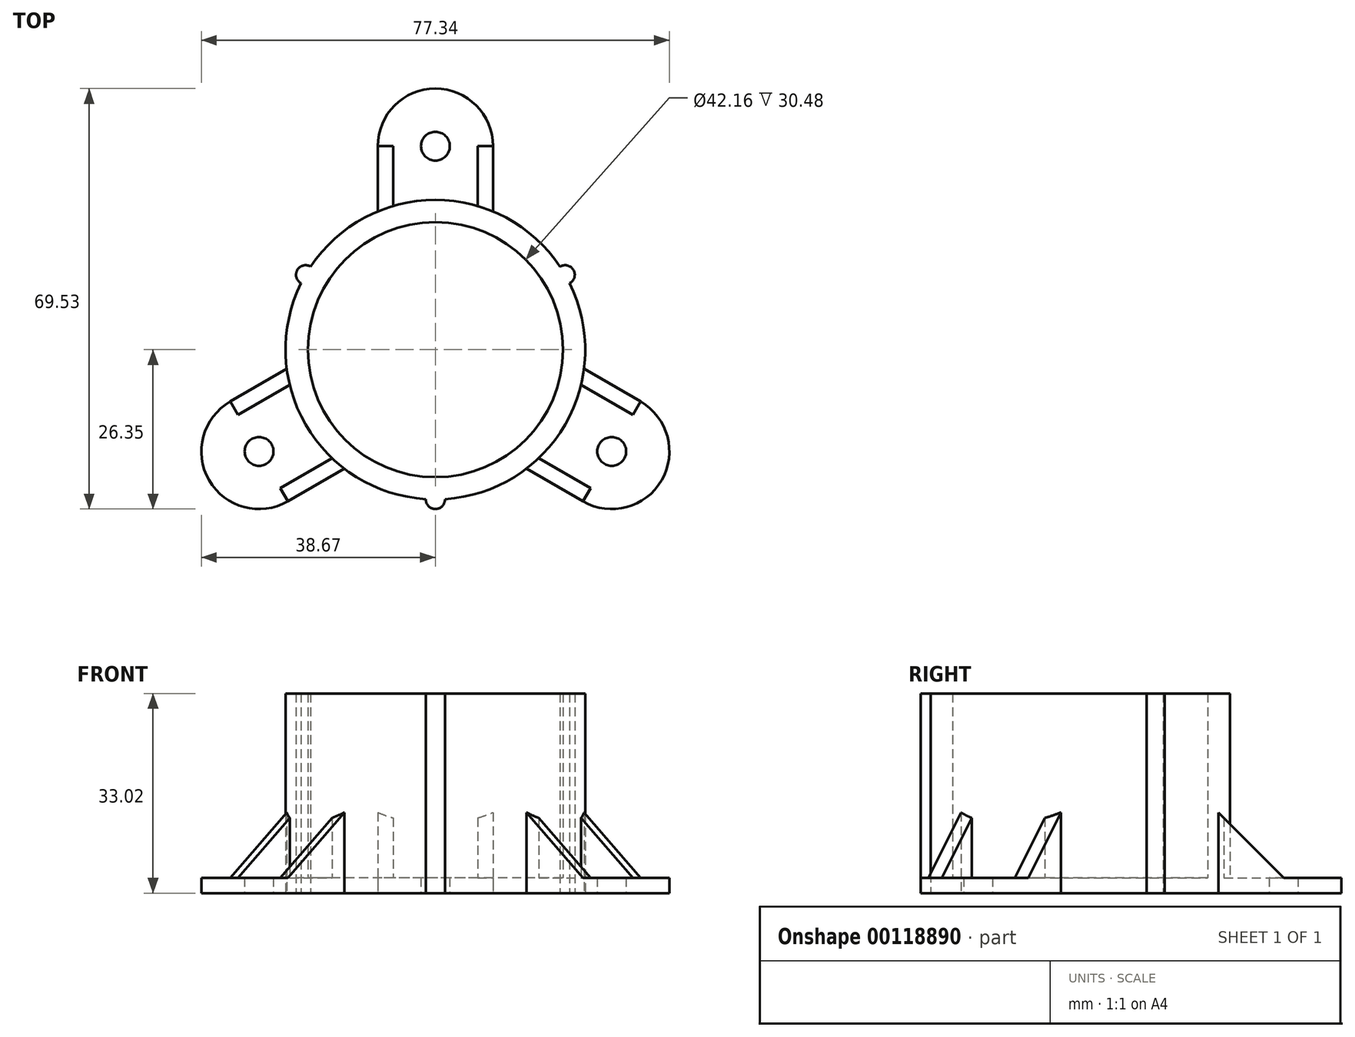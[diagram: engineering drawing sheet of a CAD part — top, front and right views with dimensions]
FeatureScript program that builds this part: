
annotation { "Feature Type Name" : "Feature", "Feature Type Description" : "" }
export const myFeature = defineFeature(function(context is Context, id is Id, definition is map)
    precondition{}
    {
        {
            var Q0;
            Q0=qCreatedBy(makeId("Top.planeOp"),FACE);
            var sketch = newSketch(context, id + "F0", { "sketchPlane" : qUnion([Q0])});
            skCircle(sketch, "E0", {"center": v(0, 0) * mm, "radius": 21.08 * mm});
            skCircle(sketch, "E1", {"center": v(0, 0) * mm, "radius": 24.77 * mm});
            skCircle(sketch, "E2", {"center": v(0, -24.77) * mm, "radius": 1.59 * mm});
            skCircle(sketch, "E3.1.0", {"center": v(21.45, 12.38) * mm, "radius": 1.59 * mm});
            skCircle(sketch, "E3.2.0", {"center": v(-21.45, 12.38) * mm, "radius": 1.59 * mm});
            skLineSegment(sketch, "E4.bottom", {"start": v(-9.53, 22.86) * mm, "end": v(9.53, 22.86) * mm});
            skLineSegment(sketch, "E4.top", {"start": v(0, 43.18) * mm, "end": v(0, 43.18) * mm});
            skLineSegment(sketch, "E4.left", {"start": v(-9.53, 22.86) * mm, "end": v(-9.53, 33.66) * mm});
            skLineSegment(sketch, "E4.right", {"start": v(9.52, 22.86) * mm, "end": v(9.52, 33.66) * mm});
            skLineSegment(sketch, "E5", {"start": v(0, 13) * mm, "end": v(0, 41.76) * mm, "construction": true});
            skPoint(sketch, "E6.visualSharp", {"position": v(-9.53, 43.18) * mm});
            skArc(sketch, "E6.filletArc", {"start": v(0, 43.18) * mm, "mid": v(-6.74, 40.4) * mm, "end": v(-9.53, 33.66) * mm});
            skPoint(sketch, "E7.visualSharp", {"position": v(9.53, 43.18) * mm});
            skArc(sketch, "E7.filletArc", {"start": v(9.53, 33.66) * mm, "mid": v(6.74, 40.4) * mm, "end": v(0, 43.18) * mm});
            skCircle(sketch, "E8", {"center": v(0, 33.66) * mm, "radius": 2.38 * mm});
            skArc(sketch, "E9.1.0", {"start": v(-33.9, -8.58) * mm, "mid": v(-38.35, -14.36) * mm, "end": v(-37.4, -21.59) * mm});
            skArc(sketch, "E9.1.1", {"start": v(-37.4, -21.6) * mm, "mid": v(-31.61, -26.03) * mm, "end": v(-24.38, -25.08) * mm});
            skCircle(sketch, "E9.1.2", {"center": v(-29.15, -16.83) * mm, "radius": 2.38 * mm});
            skLineSegment(sketch, "E9.1.3", {"start": v(-24.56, -3.18) * mm, "end": v(-33.9, -8.58) * mm});
            skLineSegment(sketch, "E9.1.4", {"start": v(-15.03, -19.68) * mm, "end": v(-24.38, -25.08) * mm});
            skLineSegment(sketch, "E9.1.5", {"start": v(-15.03, -19.68) * mm, "end": v(-24.56, -3.18) * mm});
            skArc(sketch, "E9.2.0", {"start": v(24.38, -25.08) * mm, "mid": v(31.61, -26.03) * mm, "end": v(37.4, -21.6) * mm});
            skArc(sketch, "E9.2.1", {"start": v(37.4, -21.6) * mm, "mid": v(38.35, -14.36) * mm, "end": v(33.9, -8.58) * mm});
            skCircle(sketch, "E9.2.2", {"center": v(29.15, -16.83) * mm, "radius": 2.38 * mm});
            skLineSegment(sketch, "E9.2.3", {"start": v(15.03, -19.68) * mm, "end": v(24.38, -25.08) * mm});
            skLineSegment(sketch, "E9.2.4", {"start": v(24.56, -3.18) * mm, "end": v(33.9, -8.58) * mm});
            skLineSegment(sketch, "E9.2.5", {"start": v(24.56, -3.18) * mm, "end": v(15.03, -19.68) * mm});
            skSolve(sketch);
        }
        {
            var Q0;
            Q0=qSketchRegion(id+"F0",true);
            var Q1;
            Q1=makeQuery(id+"F0.imprint","IMPRINT",FACE,{"disambiguationData":[TD([[makeQuery(id+"F0.imprint","IMPRINT",EDGE,{"derivedFrom":sQuery(id+"F0.wireOp",EDGE,"E0")}),1.0]])]});
            extrude(context, id + "F1", {"entities" : qUnion([Q0, Q1]), "depth" : 2.54 * mm});
        }
        {
            var Q0;
            Q0=makeQuery(id+"F0.imprint","IMPRINT",FACE,{"disambiguationData":[TD([[makeQuery(id+"F0.imprint","IMPRINT",EDGE,{"derivedFrom":sQuery(id+"F0.wireOp",EDGE,"E0")}),-1.0]])]});
            var Q1;
            {var subQ0=sQuery(id+"F0.wireOp",EDGE,"E9.1.5");Q1=makeQuery(id+"F0.imprint","IMPRINT",FACE,{"disambiguationData":[TD([[makeQuery(id+"F0.imprint","IMPRINT",EDGE,{"derivedFrom":subQ0}),1.0]])]});}
            var Q2;
            {var subQ0=sQuery(id+"F0.wireOp",EDGE,"E3.2.0");var subQ1=sQuery(id+"F0.wireOp",EDGE,"E1");var subQ2=makeQuery(id+"F0.imprint","INTERSECT",VERTEX,{"disambiguationData":[OD(0.0)],"derivedFrom":[subQ1,subQ0]});Q2=makeQuery(id+"F0.imprint","IMPRINT",FACE,{"disambiguationData":[TD([[makeQuery(id+"F0.imprint","IMPRINT",EDGE,{"disambiguationData":[TD([[subQ2,-1.0]])],"derivedFrom":subQ1}),1.0]])]});}
            var Q3;
            {var subQ0=sQuery(id+"F0.wireOp",EDGE,"E3.2.0");var subQ1=sQuery(id+"F0.wireOp",EDGE,"E1");var subQ2=makeQuery(id+"F0.imprint","INTERSECT",VERTEX,{"disambiguationData":[OD(0.0)],"derivedFrom":[subQ1,subQ0]});Q3=makeQuery(id+"F0.imprint","IMPRINT",FACE,{"disambiguationData":[TD([[makeQuery(id+"F0.imprint","IMPRINT",EDGE,{"disambiguationData":[TD([[subQ2,-1.0]])],"derivedFrom":subQ1}),-1.0]])]});}
            var Q4;
            {var subQ0=sQuery(id+"F0.wireOp",EDGE,"E3.1.0");var subQ1=sQuery(id+"F0.wireOp",EDGE,"E1");var subQ2=makeQuery(id+"F0.imprint","INTERSECT",VERTEX,{"disambiguationData":[OD(0.0)],"derivedFrom":[subQ1,subQ0]});Q4=makeQuery(id+"F0.imprint","IMPRINT",FACE,{"disambiguationData":[TD([[makeQuery(id+"F0.imprint","IMPRINT",EDGE,{"disambiguationData":[TD([[subQ2,1.0]])],"derivedFrom":subQ1}),1.0]])]});}
            var Q5;
            {var subQ0=sQuery(id+"F0.wireOp",EDGE,"E3.1.0");var subQ1=sQuery(id+"F0.wireOp",EDGE,"E1");var subQ2=makeQuery(id+"F0.imprint","INTERSECT",VERTEX,{"disambiguationData":[OD(0.0)],"derivedFrom":[subQ1,subQ0]});Q5=makeQuery(id+"F0.imprint","IMPRINT",FACE,{"disambiguationData":[TD([[makeQuery(id+"F0.imprint","IMPRINT",EDGE,{"disambiguationData":[TD([[subQ2,1.0]])],"derivedFrom":subQ1}),-1.0]])]});}
            var Q6;
            {var subQ0=sQuery(id+"F0.wireOp",EDGE,"E2");var subQ1=sQuery(id+"F0.wireOp",EDGE,"E1");var subQ2=makeQuery(id+"F0.imprint","INTERSECT",VERTEX,{"disambiguationData":[OD(0.0)],"derivedFrom":[subQ1,subQ0]});Q6=makeQuery(id+"F0.imprint","IMPRINT",FACE,{"disambiguationData":[TD([[makeQuery(id+"F0.imprint","IMPRINT",EDGE,{"disambiguationData":[TD([[subQ2,-1.0]])],"derivedFrom":subQ1}),-1.0]])]});}
            var Q7;
            {var subQ0=sQuery(id+"F0.wireOp",EDGE,"E2");var subQ1=sQuery(id+"F0.wireOp",EDGE,"E1");var subQ2=makeQuery(id+"F0.imprint","INTERSECT",VERTEX,{"disambiguationData":[OD(0.0)],"derivedFrom":[subQ1,subQ0]});Q7=makeQuery(id+"F0.imprint","IMPRINT",FACE,{"disambiguationData":[TD([[makeQuery(id+"F0.imprint","IMPRINT",EDGE,{"disambiguationData":[TD([[subQ2,-1.0]])],"derivedFrom":subQ1}),1.0]])]});}
            var Q8;
            {var subQ0=sQuery(id+"F0.wireOp",EDGE,"E4.bottom");Q8=makeQuery(id+"F0.imprint","IMPRINT",FACE,{"disambiguationData":[TD([[makeQuery(id+"F0.imprint","IMPRINT",EDGE,{"derivedFrom":subQ0}),1.0]])]});}
            var Q9;
            {var subQ0=sQuery(id+"F0.wireOp",EDGE,"E9.2.5");Q9=makeQuery(id+"F0.imprint","IMPRINT",FACE,{"disambiguationData":[TD([[makeQuery(id+"F0.imprint","IMPRINT",EDGE,{"derivedFrom":subQ0}),1.0]])]});}
            extrude(context, id + "F2", {"entities" : qUnion([Q0, Q1, Q2, Q3, Q4, Q5, Q6, Q7, Q8, Q9]), "operationType" : NewBodyOperationType.ADD, "depth" : 33.02 * mm});
        }
        {
            var Q0;
            Q0=makeQuery(id+"F1.opExtrude","SWEPT_FACE",FACE,{"disambiguationData":[OSD([sQuery(id+"F0.wireOp",EDGE,"E4.right")])]});
            var sketch = newSketch(context, id + "F3", { "sketchPlane" : qUnion([Q0])});
            skLineSegment(sketch, "E10.0", {"start": v(22.86, 2.54) * mm, "end": v(33.66, 2.54) * mm});
            skLineSegment(sketch, "E11", {"start": v(22.86, 2.54) * mm, "end": v(22.86, 13.33) * mm});
            skLineSegment(sketch, "E12", {"start": v(22.86, 13.33) * mm, "end": v(33.66, 2.54) * mm});
            skSolve(sketch);
        }
        {
            var Q0;
            Q0=qSketchRegion(id+"F3",true);
            extrude(context, id + "F4", {"entities" : qUnion([Q0]), "oppositeDirection" : true, "depth" : 2.54 * mm});
        }
        {
            var Q0;
            Q0=makeQuery(id+"F4.opExtrude","SWEPT_BODY",BODY,{"disambiguationData":[OSD([sQuery(id+"F3.wireOp",EDGE,"E10.0"),sQuery(id+"F3.wireOp",EDGE,"E11"),sQuery(id+"F3.wireOp",EDGE,"E12")])]});
            var Q1;
            Q1=qCreatedBy(makeId("Right.planeOp"),FACE);
            mirror(context, id + "F5", {"entities" : qUnion([Q0]), "mirrorPlane" : qUnion([Q1])});
        }
        {
            var Q0;
            Q0=makeQuery(id+"F4.opExtrude","SWEPT_BODY",BODY,{"disambiguationData":[OSD([sQuery(id+"F3.wireOp",EDGE,"E10.0"),sQuery(id+"F3.wireOp",EDGE,"E11"),sQuery(id+"F3.wireOp",EDGE,"E12")])]});
            var Q1;
            Q1=makeQuery(id+"F5.opPattern","COPY",BODY,{"derivedFrom":makeQuery(id+"F4.opExtrude","SWEPT_BODY",BODY,{"disambiguationData":[OSD([sQuery(id+"F3.wireOp",EDGE,"E10.0"),sQuery(id+"F3.wireOp",EDGE,"E11"),sQuery(id+"F3.wireOp",EDGE,"E12")])]}),"instanceName":"1"});
            var Q2;
            Q2=makeQuery(id+"F2.boolean.opBoolean","INTERSECT",EDGE,{"derivedFrom":[makeQuery(id+"F1.opExtrude","CAP_FACE",FACE,{"disambiguationData":[OSD([sQuery(id+"F0.wireOp",EDGE,"E1"),sQuery(id+"F0.wireOp",EDGE,"E2"),sQuery(id+"F0.wireOp",EDGE,"E3.1.0"),sQuery(id+"F0.wireOp",EDGE,"E3.2.0"),sQuery(id+"F0.wireOp",EDGE,"E4.left"),sQuery(id+"F0.wireOp",EDGE,"E4.right"),sQuery(id+"F0.wireOp",EDGE,"E6.filletArc"),sQuery(id+"F0.wireOp",EDGE,"E7.filletArc"),sQuery(id+"F0.wireOp",EDGE,"E8"),sQuery(id+"F0.wireOp",EDGE,"E9.1.0"),sQuery(id+"F0.wireOp",EDGE,"E9.1.1"),sQuery(id+"F0.wireOp",EDGE,"E9.1.2"),sQuery(id+"F0.wireOp",EDGE,"E9.1.3"),sQuery(id+"F0.wireOp",EDGE,"E9.1.4"),sQuery(id+"F0.wireOp",EDGE,"E9.2.0"),sQuery(id+"F0.wireOp",EDGE,"E9.2.1"),sQuery(id+"F0.wireOp",EDGE,"E9.2.2"),sQuery(id+"F0.wireOp",EDGE,"E9.2.3"),sQuery(id+"F0.wireOp",EDGE,"E9.2.4")])],"isStart":false}),makeQuery(id+"F2.opExtrude","SWEPT_FACE",FACE,{"disambiguationData":[OSD([sQuery(id+"F0.wireOp",EDGE,"E0")])]})]});
            circularPattern(context, id + "F6", {"operationType" : NewBodyOperationType.ADD, "entities" : qUnion([Q0, Q1]), "axis" : qUnion([Q2]), "angle" : 120 * degree, "instanceCount" : 3});
        }
    });
